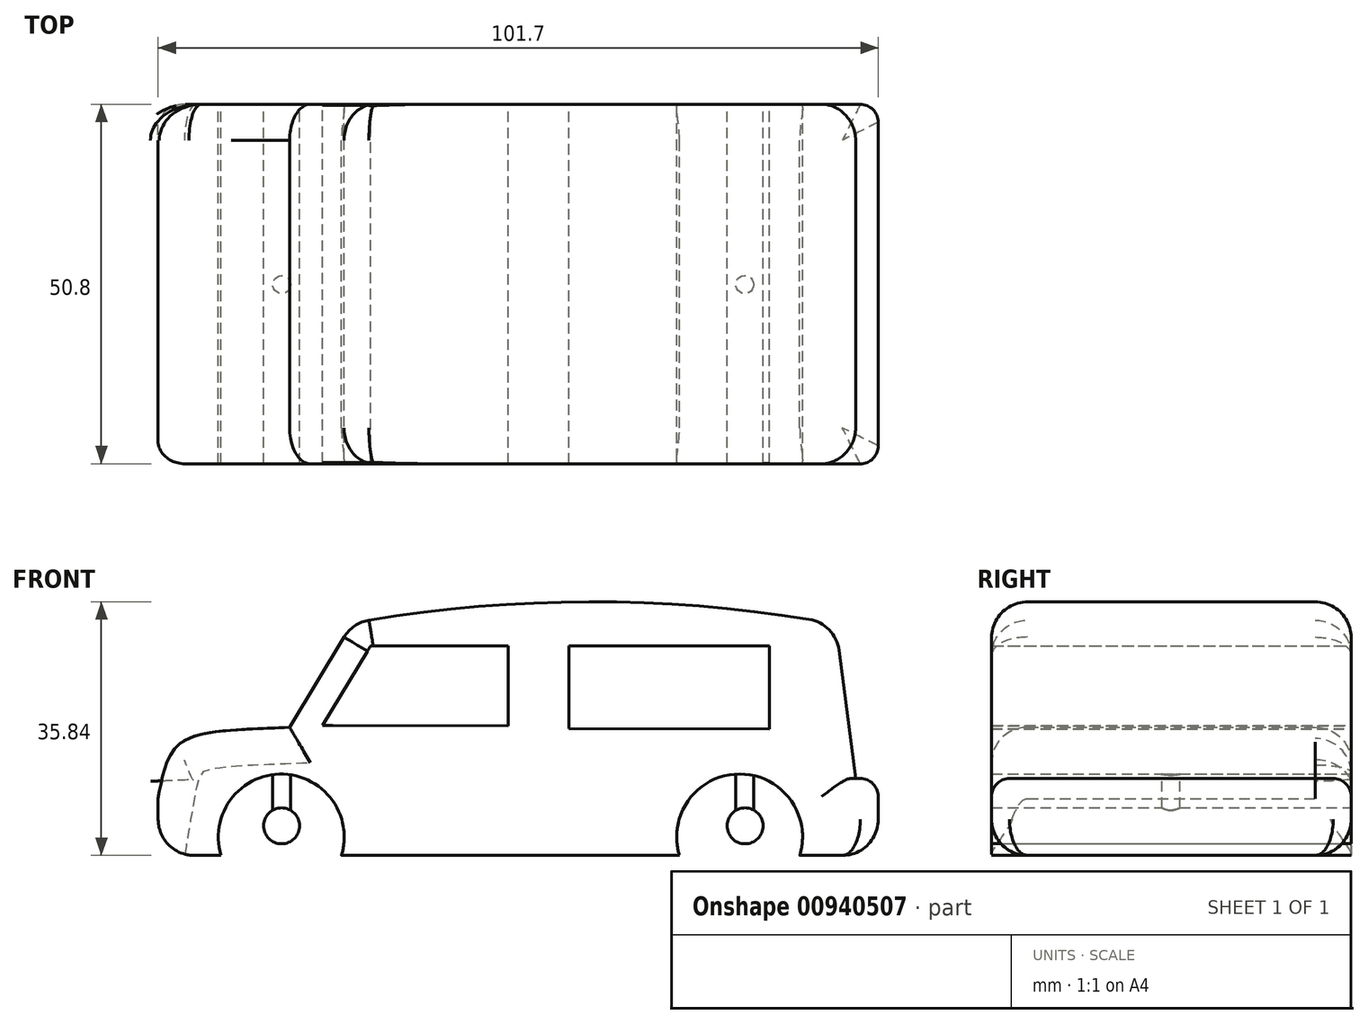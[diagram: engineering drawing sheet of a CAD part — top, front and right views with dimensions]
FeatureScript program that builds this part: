
annotation { "Feature Type Name" : "Feature", "Feature Type Description" : "" }
export const myFeature = defineFeature(function(context is Context, id is Id, definition is map)
    precondition{}
    {
        {
            var Q0;
            Q0=qCreatedBy(makeId("Front.planeOp"),FACE);
            var sketch = newSketch(context, id + "F0", { "sketchPlane" : qUnion([Q0])});
            skFitSpline(sketch, "E0", {"points": [v(-45.85, 0) * mm, v(-27.29, 10.07) * mm], "startDerivative": vector(4.83, 28.44) * mm, "endDerivative": vector(46.68, 1.76) * mm});
            skLineSegment(sketch, "E1", {"start": v(-45.85, 0) * mm, "end": v(-45.85, -8.03) * mm});
            skLineSegment(sketch, "E2", {"start": v(-45.85, -8.03) * mm, "end": v(-36.97, -8.03) * mm});
            skArc(sketch, "E3", {"start": v(-19.97, -8.03) * mm, "mid": v(-28.47, 3.46) * mm, "end": v(-36.97, -8.03) * mm});
            skLineSegment(sketch, "E4", {"start": v(-19.97, -8.03) * mm, "end": v(27.77, -8.03) * mm});
            skLineSegment(sketch, "E5", {"start": v(-36.97, -8.03) * mm, "end": v(-19.97, -8.03) * mm});
            skLineSegment(sketch, "E6", {"start": v(27.77, -8.03) * mm, "end": v(44.77, -8.03) * mm});
            skArc(sketch, "E7", {"start": v(44.77, -8.03) * mm, "mid": v(36.27, 3.48) * mm, "end": v(27.77, -8.03) * mm});
            skLineSegment(sketch, "E8", {"start": v(44.77, -8.03) * mm, "end": v(52.07, -8.03) * mm});
            skLineSegment(sketch, "E9", {"start": v(52.07, 7.4) * mm, "end": v(49.82, 24.67) * mm});
            skLineSegment(sketch, "E10", {"start": v(49.82, 24.67) * mm, "end": v(53.57, 25.16) * mm});
            skLineSegment(sketch, "E11", {"start": v(49.82, 24.67) * mm, "end": v(-74.28, 24.92) * mm, "construction": true});
            skPoint(sketch, "E11.endSnap0", {"position": v(51.7, 24.92) * mm});
            skLineSegment(sketch, "E12", {"start": v(-27.29, 10.07) * mm, "end": v(-18.4, 24.8) * mm});
            skArc(sketch, "E13", {"start": v(49.82, 24.67) * mm, "mid": v(15.72, 27.8) * mm, "end": v(-18.4, 24.8) * mm});
            skLineSegment(sketch, "E14", {"start": v(52.07, 7.4) * mm, "end": v(52.66, 2.83) * mm});
            skLineSegment(sketch, "E15", {"start": v(52.66, 2.83) * mm, "end": v(55.85, 2.83) * mm});
            skLineSegment(sketch, "E16", {"start": v(55.85, 2.83) * mm, "end": v(55.85, -8.03) * mm});
            skLineSegment(sketch, "E17", {"start": v(52.07, -8.03) * mm, "end": v(55.85, -8.03) * mm});
            skPoint(sketch, "E18.orphan", {"position": v(55.85, -8.71) * mm});
            skArc(sketch, "E19", {"start": v(-5.43, 27.4) * mm, "mid": v(-6.19, 27.13) * mm, "end": v(-6.73, 26.53) * mm});
            skArc(sketch, "E20", {"start": v(38.12, 27.8) * mm, "mid": v(16.33, 29.45) * mm, "end": v(-5.43, 27.4) * mm});
            skPoint(sketch, "E20.startSnap0", {"position": v(15.72, 27.8) * mm});
            skArc(sketch, "E21", {"start": v(39.37, 26.3) * mm, "mid": v(38.87, 27.15) * mm, "end": v(38.12, 27.8) * mm});
            skArc(sketch, "E22", {"start": v(-5.43, 28.03) * mm, "mid": v(-7.53, 27.29) * mm, "end": v(-9.47, 26.2) * mm});
            skArc(sketch, "E23", {"start": v(41.6, 26) * mm, "mid": v(40.04, 27.47) * mm, "end": v(38.12, 28.41) * mm});
            skArc(sketch, "E24", {"start": v(38.12, 28.41) * mm, "mid": v(16.54, 29.9) * mm, "end": v(-5, 28.03) * mm});
            skLineSegment(sketch, "E25", {"start": v(-5.43, 28.03) * mm, "end": v(-5, 28.03) * mm});
            skLineSegment(sketch, "E26", {"start": v(-22.63, 10.34) * mm, "end": v(-15.84, 21.6) * mm});
            skLineSegment(sketch, "E27", {"start": v(-15.84, 21.6) * mm, "end": v(3.57, 21.57) * mm});
            skLineSegment(sketch, "E28", {"start": v(-22.63, 10.34) * mm, "end": v(3.57, 10.29) * mm});
            skLineSegment(sketch, "E29", {"start": v(3.57, 21.57) * mm, "end": v(3.57, 10.29) * mm});
            skLineSegment(sketch, "E30", {"start": v(12.16, 21.57) * mm, "end": v(12.16, 9.88) * mm});
            skLineSegment(sketch, "E31", {"start": v(12.16, 9.88) * mm, "end": v(40.48, 9.83) * mm});
            skLineSegment(sketch, "E32", {"start": v(40.48, 9.83) * mm, "end": v(40.48, 21.57) * mm});
            skLineSegment(sketch, "E33", {"start": v(40.48, 21.57) * mm, "end": v(12.16, 21.57) * mm});
            skSolve(sketch);
        }
        {
            var Q0;
            Q0=makeQuery(id+"F0.imprint","IMPRINT",FACE,{"disambiguationData":[TD([[makeQuery(id+"F0.imprint","IMPRINT",EDGE,{"derivedFrom":sQuery(id+"F0.wireOp",EDGE,"E0")}),-1.0]])]});
            extrude(context, id + "F1", {"entities" : qUnion([Q0]), "depth" : 50.8 * mm, "offsetDistance" : 25.4 * mm});
        }
        {
            var Q0;
            Q0=makeQuery(id+"F1.opExtrude","CAP_EDGE",EDGE,{"disambiguationData":[OSD([sQuery(id+"F0.wireOp",EDGE,"E12")])],"isStart":false});
            var Q1;
            Q1=makeQuery(id+"F1.opExtrude","CAP_EDGE",EDGE,{"disambiguationData":[OSD([sQuery(id+"F0.wireOp",EDGE,"E12")])],"isStart":true});
            var Q2;
            {var subQ0=sQuery(id+"F0.wireOp",EDGE,"E13");Q2=makeQuery(id+"F1.opExtrude","CAP_EDGE",EDGE,{"disambiguationData":[OSD([subQ0]),TDD([makeQuery(id+"F0.imprint","IMPRINT",EDGE,{"disambiguationData":[TD([[makeQuery(id+"F0.imprint","INTERSECT",VERTEX,{"derivedFrom":[sQuery(id+"F0.wireOp",EDGE,"E12"),subQ0]}),1.0]])],"derivedFrom":subQ0})])],"isStart":false});}
            var Q3;
            {var subQ0=sQuery(id+"F0.wireOp",EDGE,"E13");Q3=makeQuery(id+"F1.opExtrude","CAP_EDGE",EDGE,{"disambiguationData":[OSD([subQ0]),TDD([makeQuery(id+"F0.imprint","IMPRINT",EDGE,{"disambiguationData":[TD([[makeQuery(id+"F0.imprint","INTERSECT",VERTEX,{"derivedFrom":[sQuery(id+"F0.wireOp",EDGE,"E12"),subQ0]}),1.0]])],"derivedFrom":subQ0})])],"isStart":true});}
            fillet(context, id + "F2", {"entities" : qUnion([Q0, Q1, Q2, Q3]), "radius" : 5.08 * mm, "tangentPropagation" : true, "allowEdgeOverflow" : false});
        }
        {
            var Q0;
            Q0=makeQuery(id+"F1.opExtrude","SWEPT_EDGE",EDGE,{"disambiguationData":[OSD([sQuery(id+"F0.wireOp",EDGE,"E9"),sQuery(id+"F0.wireOp",EDGE,"E13")])]});
            fillet(context, id + "F3", {"entities" : qUnion([Q0]), "radius" : 5.08 * mm, "tangentPropagation" : true, "allowEdgeOverflow" : false});
        }
        {
            var Q0;
            Q0=makeQuery(id+"F1.opExtrude","CAP_EDGE",EDGE,{"disambiguationData":[OSD([sQuery(id+"F0.wireOp",EDGE,"E15")])],"isStart":false});
            var Q1;
            Q1=makeQuery(id+"F1.opExtrude","SWEPT_EDGE",EDGE,{"disambiguationData":[OSD([sQuery(id+"F0.wireOp",EDGE,"E15"),sQuery(id+"F0.wireOp",EDGE,"E16")])]});
            var Q2;
            Q2=makeQuery(id+"F1.opExtrude","CAP_EDGE",EDGE,{"disambiguationData":[OSD([sQuery(id+"F0.wireOp",EDGE,"E15")])],"isStart":true});
            var Q3;
            Q3=makeQuery(id+"F1.opExtrude","CAP_EDGE",EDGE,{"disambiguationData":[OSD([sQuery(id+"F0.wireOp",EDGE,"E16")])],"isStart":false});
            var Q4;
            Q4=makeQuery(id+"F1.opExtrude","CAP_EDGE",EDGE,{"disambiguationData":[OSD([sQuery(id+"F0.wireOp",EDGE,"E16")])],"isStart":true});
            fillet(context, id + "F4", {"entities" : qUnion([Q0, Q1, Q2, Q3, Q4]), "radius" : 2.54 * mm, "tangentPropagation" : true, "allowEdgeOverflow" : false});
        }
        {
            var Q0;
            Q0=makeQuery(id+"F1.opExtrude","CAP_EDGE",EDGE,{"disambiguationData":[OSD([sQuery(id+"F0.wireOp",EDGE,"E0")])],"isStart":false});
            var Q1;
            Q1=makeQuery(id+"F1.opExtrude","CAP_EDGE",EDGE,{"disambiguationData":[OSD([sQuery(id+"F0.wireOp",EDGE,"E0")])],"isStart":true});
            fillet(context, id + "F5", {"entities" : qUnion([Q0, Q1]), "radius" : 5.08 * mm, "tangentPropagation" : true, "allowEdgeOverflow" : false});
        }
        {
            var Q0;
            Q0=makeQuery(id+"F1.opExtrude","SWEPT_EDGE",EDGE,{"disambiguationData":[OSD([sQuery(id+"F0.wireOp",EDGE,"E12"),sQuery(id+"F0.wireOp",EDGE,"E13")])]});
            fillet(context, id + "F6", {"entities" : qUnion([Q0]), "radius" : 5.08 * mm, "tangentPropagation" : true, "allowEdgeOverflow" : false});
        }
        {
            var Q0;
            Q0=qCreatedBy(makeId("Top.planeOp"),FACE);
            var sketch = newSketch(context, id + "F7", { "sketchPlane" : qUnion([Q0])});
            skLineSegment(sketch, "E34", {"start": v(0, 0) * mm, "end": v(0, -50.95) * mm});
            skLineSegment(sketch, "E35", {"start": v(-36.99, -28.26) * mm, "end": v(-19.82, -28.26) * mm});
            skPoint(sketch, "E36", {"position": v(-19.83, -25.47) * mm});
            skPoint(sketch, "E36.positionSnap0", {"position": v(0, -25.47) * mm});
            skPoint(sketch, "E37", {"position": v(-28.4, -28.26) * mm});
            skCircle(sketch, "E38", {"center": v(-28.4, -25.47) * mm, "radius": 1.27 * mm});
            skLineSegment(sketch, "E39", {"start": v(36.99, -28.26) * mm, "end": v(44.85, -28.26) * mm});
            skLineSegment(sketch, "E40", {"start": v(44.85, -28.26) * mm, "end": v(27.73, -28.26) * mm});
            skCircle(sketch, "E41", {"center": v(36.99, -25.47) * mm, "radius": 1.27 * mm});
            skSolve(sketch);
        }
        {
            var Q0;
            Q0 = qSketchRegion(id + "F7", true);
            extrude(context, id + "F8", {"entities" : qUnion([Q0]), "operationType" : NewBodyOperationType.ADD, "endBound" : BoundingType.SYMMETRIC, "oppositeDirection" : true, "depth" : 7.62 * mm, "offsetDistance" : 25.4 * mm});
        }
        {
            var Q0;
            Q0=qCreatedBy(makeId("Front.planeOp"),FACE);
            var sketch = newSketch(context, id + "F9", { "sketchPlane" : qUnion([Q0])});
            skCircle(sketch, "E42", {"center": v(-28.42, -3.85) * mm, "radius": 2.54 * mm});
            skCircle(sketch, "E43", {"center": v(37.04, -3.85) * mm, "radius": 2.54 * mm});
            skSolve(sketch);
        }
        {
            var Q0;
            Q0 = qSketchRegion(id + "F9", true);
            extrude(context, id + "F10", {"entities" : qUnion([Q0]), "operationType" : NewBodyOperationType.ADD, "depth" : 50.8 * mm, "offsetDistance" : 25.4 * mm});
        }
        {
            var Q0;
            Q0=makeQuery(id+"F1.opExtrude","CAP_EDGE",EDGE,{"disambiguationData":[OSD([sQuery(id+"F0.wireOp",EDGE,"E4")])],"isStart":false});
            var Q1;
            Q1=makeQuery(id+"F1.opExtrude","CAP_EDGE",EDGE,{"disambiguationData":[OSD([sQuery(id+"F0.wireOp",EDGE,"E8"),sQuery(id+"F0.wireOp",EDGE,"E17")])],"isStart":false});
            var Q2;
            Q2=makeQuery(id+"F1.opExtrude","CAP_EDGE",EDGE,{"disambiguationData":[OSD([sQuery(id+"F0.wireOp",EDGE,"E4")])],"isStart":true});
            var Q3;
            Q3=makeQuery(id+"F1.opExtrude","CAP_EDGE",EDGE,{"disambiguationData":[OSD([sQuery(id+"F0.wireOp",EDGE,"E8"),sQuery(id+"F0.wireOp",EDGE,"E17")])],"isStart":true});
            fillet(context, id + "F11", {"entities" : qUnion([Q0, Q1, Q2, Q3]), "radius" : 5.08 * mm, "tangentPropagation" : true, "allowEdgeOverflow" : false});
        }
        {
            var Q0;
            Q0=makeQuery(id+"F1.opExtrude","SWEPT_EDGE",EDGE,{"disambiguationData":[OSD([sQuery(id+"F0.wireOp",EDGE,"E1"),sQuery(id+"F0.wireOp",EDGE,"E2")])]});
            fillet(context, id + "F12", {"entities" : qUnion([Q0]), "radius" : 5.08 * mm, "tangentPropagation" : true, "allowEdgeOverflow" : false});
        }
    });
